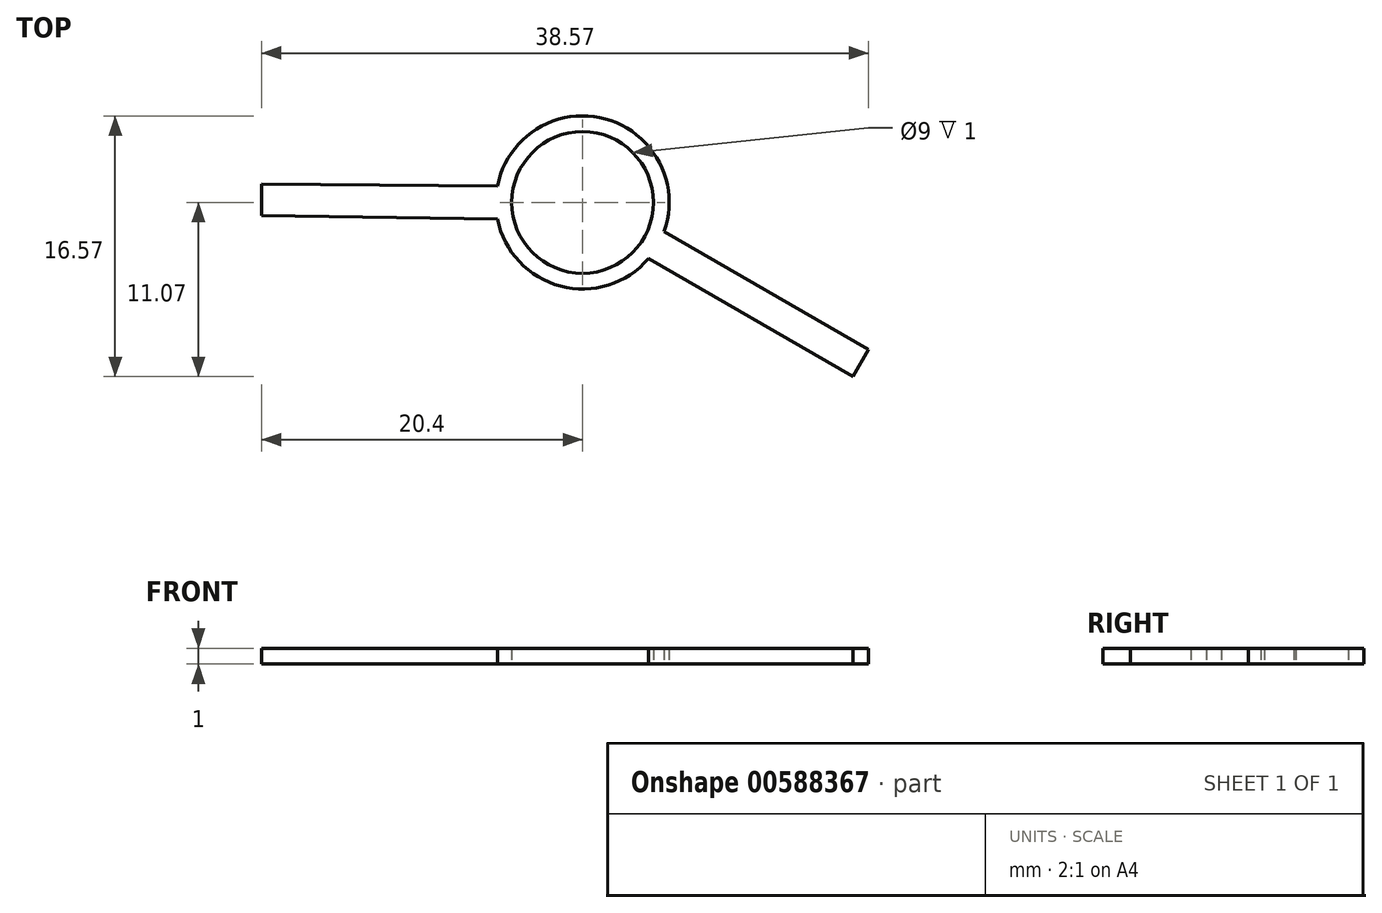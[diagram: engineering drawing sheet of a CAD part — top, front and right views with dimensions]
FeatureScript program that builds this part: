
annotation { "Feature Type Name" : "Feature", "Feature Type Description" : "" }
export const myFeature = defineFeature(function(context is Context, id is Id, definition is map)
    precondition{}
    {
        {
            var Q0;
            Q0=qCreatedBy(makeId("Top.planeOp"),FACE);
            var sketch = newSketch(context, id + "F0", { "sketchPlane" : qUnion([Q0])});
            skCircle(sketch, "E0", {"center": v(0, 0) * mm, "radius": 4.5 * mm});
            skArc(sketch, "E1", {"start": v(-5.4, -1.05) * mm, "mid": v(-1.4, -5.32) * mm, "end": v(4.18, -3.57) * mm});
            skLineSegment(sketch, "E2.right", {"start": v(-20.4, -0.84) * mm, "end": v(-20.4, 1.16) * mm});
            skLineSegment(sketch, "E3.trimOffspring", {"start": v(-5.4, 1.05) * mm, "end": v(-20.4, 1.16) * mm});
            skLineSegment(sketch, "E4.trimOffspring", {"start": v(-5.4, -1.05) * mm, "end": v(-20.4, -0.84) * mm});
            skLineSegment(sketch, "E5.bottom", {"start": v(18.17, -9.34) * mm, "end": v(5.18, -1.84) * mm});
            skLineSegment(sketch, "E5.top", {"start": v(17.17, -11.07) * mm, "end": v(4.18, -3.57) * mm});
            skLineSegment(sketch, "E5.left", {"start": v(18.17, -9.34) * mm, "end": v(17.17, -11.07) * mm});
            skArc(sketch, "E6.trimOffspring", {"start": v(5.18, -1.84) * mm, "mid": v(1.45, 5.3) * mm, "end": v(-5.4, 1.05) * mm});
            skSolve(sketch);
        }
        {
            var Q0;
            Q0 = qSketchRegion(id + "F0", true);
            extrude(context, id + "F1", {"entities" : qUnion([Q0]), "depth" : 1 * mm, "offsetDistance" : 25.4 * mm});
        }
    });
